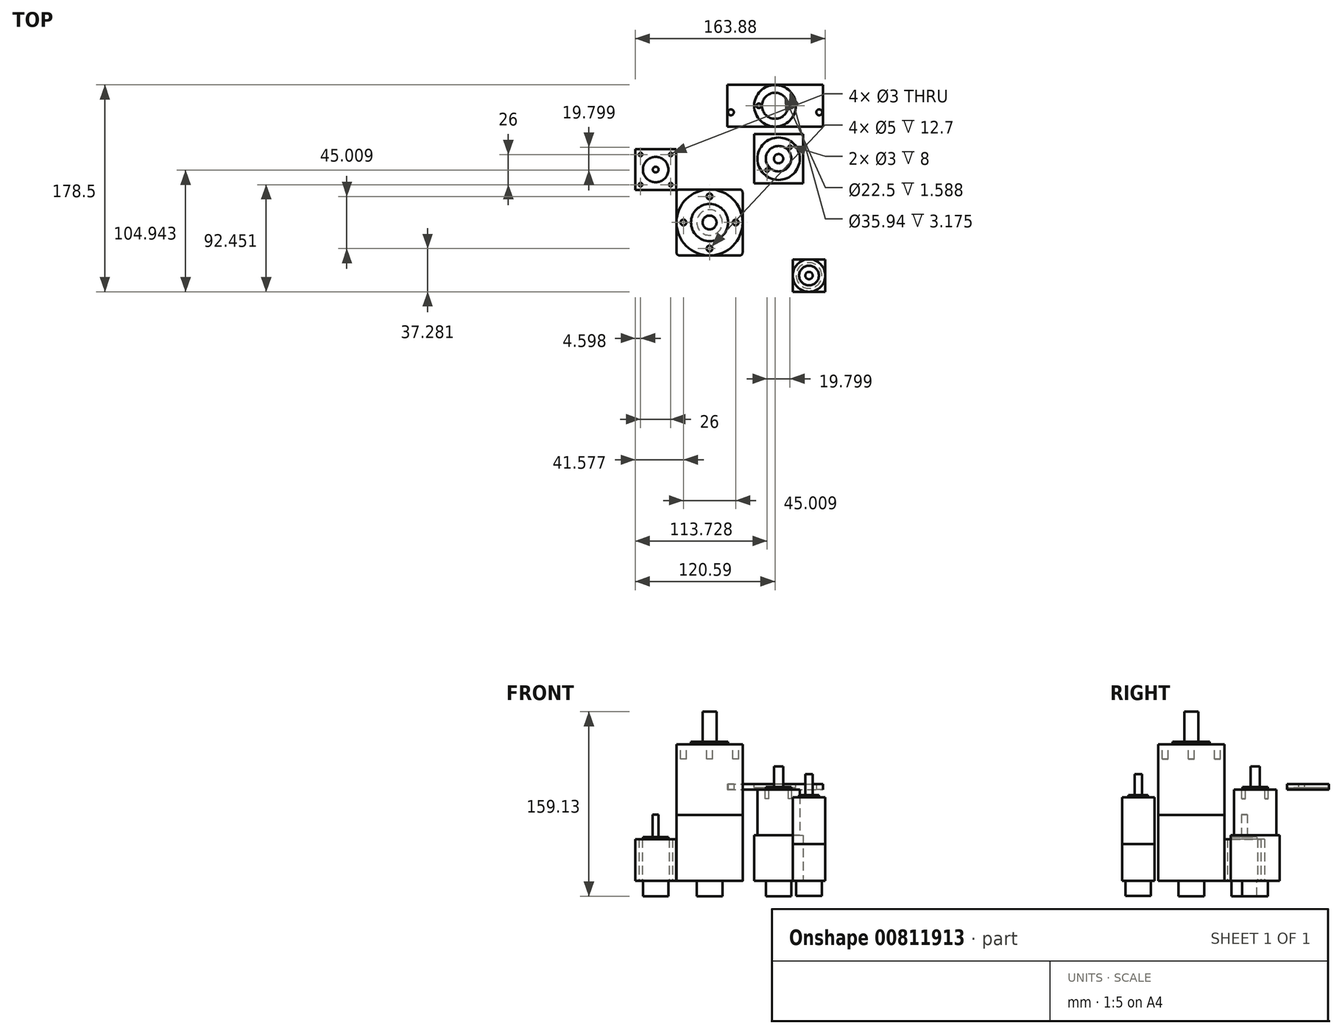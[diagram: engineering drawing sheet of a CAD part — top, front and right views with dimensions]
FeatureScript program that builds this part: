
annotation { "Feature Type Name" : "Feature", "Feature Type Description" : "" }
export const myFeature = defineFeature(function(context is Context, id is Id, definition is map)
    precondition{}
    {
        {
            var Q0;
            Q0=qCreatedBy(makeId("Top.planeOp"),FACE);
            var sketch = newSketch(context, id + "F0", { "sketchPlane" : qUnion([Q0])});
            skLineSegment(sketch, "E0.bottom", {"start": v(-20.35, 13.53) * mm, "end": v(31.57, 13.53) * mm});
            skLineSegment(sketch, "E0.top", {"start": v(-20.35, -43.46) * mm, "end": v(31.57, -43.46) * mm});
            skLineSegment(sketch, "E0.left", {"start": v(-22.89, 11) * mm, "end": v(-22.89, -40.92) * mm});
            skLineSegment(sketch, "E0.right", {"start": v(34.11, 11) * mm, "end": v(34.11, -40.92) * mm});
            skLineSegment(sketch, "E1", {"start": v(-22.89, 13.53) * mm, "end": v(34.11, -43.46) * mm, "construction": true});
            skLineSegment(sketch, "E2", {"start": v(34.11, 13.53) * mm, "end": v(-22.89, -43.46) * mm, "construction": true});
            skCircle(sketch, "E3", {"center": v(5.61, -14.96) * mm, "radius": 28.5 * mm, "construction": true});
            skPoint(sketch, "E4.visualSharp", {"position": v(-22.89, 13.53) * mm});
            skArc(sketch, "E4.filletArc", {"start": v(-20.35, 13.53) * mm, "mid": v(-22.14, 12.8) * mm, "end": v(-22.89, 11) * mm});
            skPoint(sketch, "E5.visualSharp", {"position": v(34.11, 13.53) * mm});
            skArc(sketch, "E5.filletArc", {"start": v(34.11, 11) * mm, "mid": v(33.37, 12.8) * mm, "end": v(31.57, 13.53) * mm});
            skPoint(sketch, "E6.visualSharp", {"position": v(34.11, -43.46) * mm});
            skArc(sketch, "E6.filletArc", {"start": v(31.57, -43.46) * mm, "mid": v(33.37, -42.72) * mm, "end": v(34.11, -40.92) * mm});
            skPoint(sketch, "E7.visualSharp", {"position": v(-22.89, -43.46) * mm});
            skArc(sketch, "E7.filletArc", {"start": v(-22.89, -40.92) * mm, "mid": v(-22.14, -42.72) * mm, "end": v(-20.35, -43.46) * mm});
            skSolve(sketch);
        }
        {
            var Q0;
            Q0=makeQuery(id+"F0.imprint","IMPRINT",FACE,{"disambiguationData":[TD([[makeQuery(id+"F0.imprint","IMPRINT",EDGE,{"derivedFrom":sQuery(id+"F0.wireOp",EDGE,"E0.bottom")}),-1.0]])]});
            extrude(context, id + "F1", {"entities" : qUnion([Q0]), "depth" : 57.02 * mm});
        }
        {
            var Q0;
            Q0=makeQuery(id+"F1.opExtrude","CAP_FACE",FACE,{"disambiguationData":[OSD([sQuery(id+"F0.wireOp",EDGE,"E0.bottom"),sQuery(id+"F0.wireOp",EDGE,"E0.top"),sQuery(id+"F0.wireOp",EDGE,"E0.left"),sQuery(id+"F0.wireOp",EDGE,"E0.right"),sQuery(id+"F0.wireOp",EDGE,"E4.filletArc"),sQuery(id+"F0.wireOp",EDGE,"E5.filletArc"),sQuery(id+"F0.wireOp",EDGE,"E6.filletArc"),sQuery(id+"F0.wireOp",EDGE,"E7.filletArc")])],"isStart":false});
            var sketch = newSketch(context, id + "F2", { "sketchPlane" : qUnion([Q0])});
            skCircle(sketch, "E8", {"center": v(5.61, -14.96) * mm, "radius": 28.5 * mm});
            skSolve(sketch);
        }
        {
            var Q0;
            {var subQ0=sQuery(id+"F2.wireOp",EDGE,"E8");var subQ4=makeQuery(id+"F2.imprint","INTERSECT",VERTEX,{"derivedFrom":[makeQuery(id+"F1.opExtrude","CAP_EDGE",EDGE,{"disambiguationData":[OSD([sQuery(id+"F0.wireOp",EDGE,"E0.bottom")])],"isStart":false}),subQ0]});Q0=makeQuery(id+"F2.imprint","IMPRINT",FACE,{"disambiguationData":[TD([[makeQuery(id+"F2.imprint","IMPRINT",EDGE,{"disambiguationData":[TD([[subQ4,1.0]])],"derivedFrom":subQ0}),1.0]])]});}
            extrude(context, id + "F3", {"entities" : qUnion([Q0]), "operationType" : NewBodyOperationType.ADD, "depth" : 61 * mm});
        }
        {
            var Q0;
            Q0=makeQuery(id+"F3.opExtrude","CAP_FACE",FACE,{"disambiguationData":[OSD([sQuery(id+"F2.wireOp",EDGE,"E8")])],"isStart":false});
            var sketch = newSketch(context, id + "F4", { "sketchPlane" : qUnion([Q0])});
            skCircle(sketch, "E9", {"center": v(5.61, -14.96) * mm, "radius": 16 * mm});
            skSolve(sketch);
        }
        {
            var Q0;
            Q0=makeQuery(id+"F4.imprint","IMPRINT",FACE,{"disambiguationData":[TD([[makeQuery(id+"F4.imprint","IMPRINT",EDGE,{"derivedFrom":sQuery(id+"F4.wireOp",EDGE,"E9")}),1.0]])]});
            extrude(context, id + "F5", {"entities" : qUnion([Q0]), "operationType" : NewBodyOperationType.ADD, "depth" : 2 * mm});
        }
        {
            var Q0;
            Q0=makeQuery(id+"F5.opExtrude","CAP_FACE",FACE,{"disambiguationData":[OSD([sQuery(id+"F4.wireOp",EDGE,"E9")])],"isStart":false});
            var sketch = newSketch(context, id + "F6", { "sketchPlane" : qUnion([Q0])});
            skCircle(sketch, "E10", {"center": v(5.61, -14.96) * mm, "radius": 6 * mm});
            skSolve(sketch);
        }
        {
            var Q0;
            Q0=makeQuery(id+"F6.imprint","IMPRINT",FACE,{"disambiguationData":[TD([[makeQuery(id+"F6.imprint","IMPRINT",EDGE,{"derivedFrom":sQuery(id+"F6.wireOp",EDGE,"E10")}),1.0]])]});
            extrude(context, id + "F7", {"entities" : qUnion([Q0]), "operationType" : NewBodyOperationType.ADD, "depth" : 26 * mm});
        }
        {
            var Q0;
            Q0=makeQuery(id+"F3.opExtrude","CAP_FACE",FACE,{"disambiguationData":[OSD([sQuery(id+"F2.wireOp",EDGE,"E8")])],"isStart":false});
            var sketch = newSketch(context, id + "F8", { "sketchPlane" : qUnion([Q0])});
            skCircle(sketch, "E11", {"center": v(5.61, -14.96) * mm, "radius": 22.5 * mm, "construction": true});
            skCircle(sketch, "E12", {"center": v(5.61, 7.54) * mm, "radius": 2.5 * mm});
            skCircle(sketch, "E13", {"center": v(28.12, -14.96) * mm, "radius": 2.5 * mm});
            skCircle(sketch, "E14", {"center": v(5.61, -37.47) * mm, "radius": 2.5 * mm});
            skCircle(sketch, "E15", {"center": v(-16.9, -14.96) * mm, "radius": 2.5 * mm});
            skSolve(sketch);
        }
        {
            var Q0;
            {Q0=qUnion([makeQuery(id+"F8.imprint","IMPRINT",FACE,{"disambiguationData":[TD([[makeQuery(id+"F8.imprint","IMPRINT",EDGE,{"derivedFrom":sQuery(id+"F8.wireOp",EDGE,"E12")}),1.0]])]}),makeQuery(id+"F8.imprint","IMPRINT",FACE,{"disambiguationData":[TD([[makeQuery(id+"F8.imprint","IMPRINT",EDGE,{"derivedFrom":sQuery(id+"F8.wireOp",EDGE,"E13")}),1.0]])]}),makeQuery(id+"F8.imprint","IMPRINT",FACE,{"disambiguationData":[TD([[makeQuery(id+"F8.imprint","IMPRINT",EDGE,{"derivedFrom":sQuery(id+"F8.wireOp",EDGE,"E14")}),1.0]])]}),makeQuery(id+"F8.imprint","IMPRINT",FACE,{"disambiguationData":[TD([[makeQuery(id+"F8.imprint","IMPRINT",EDGE,{"derivedFrom":sQuery(id+"F8.wireOp",EDGE,"E15")}),1.0]])]})]);}
            extrude(context, id + "F9", {"entities" : qUnion([Q0]), "operationType" : NewBodyOperationType.REMOVE, "oppositeDirection" : true, "depth" : 12.7 * mm});
        }
        {
            var Q0;
            Q0=qCreatedBy(makeId("Top.planeOp"),FACE);
            var sketch = newSketch(context, id + "F10", { "sketchPlane" : qUnion([Q0])});
            skLineSegment(sketch, "E16.bottom", {"start": v(44.01, 61.24) * mm, "end": v(86.3, 61.24) * mm});
            skLineSegment(sketch, "E16.top", {"start": v(44.01, 18.95) * mm, "end": v(86.3, 18.95) * mm});
            skLineSegment(sketch, "E16.left", {"start": v(44.01, 61.24) * mm, "end": v(44.01, 18.95) * mm});
            skLineSegment(sketch, "E16.right", {"start": v(86.3, 61.24) * mm, "end": v(86.3, 18.95) * mm});
            skSolve(sketch);
        }
        {
            var Q0;
            Q0=makeQuery(id+"F10.imprint","IMPRINT",FACE,{"disambiguationData":[TD([[makeQuery(id+"F10.imprint","IMPRINT",EDGE,{"derivedFrom":sQuery(id+"F10.wireOp",EDGE,"E16.bottom")}),-1.0]])]});
            extrude(context, id + "F11", {"entities" : qUnion([Q0]), "depth" : 39.5 * mm});
        }
        {
            var Q0;
            Q0=makeQuery(id+"F11.opExtrude","CAP_FACE",FACE,{"disambiguationData":[OSD([sQuery(id+"F10.wireOp",EDGE,"E16.bottom"),sQuery(id+"F10.wireOp",EDGE,"E16.top"),sQuery(id+"F10.wireOp",EDGE,"E16.left"),sQuery(id+"F10.wireOp",EDGE,"E16.right")])],"isStart":false});
            var sketch = newSketch(context, id + "F12", { "sketchPlane" : qUnion([Q0])});
            skCircle(sketch, "E17", {"center": v(65.16, 40.1) * mm, "radius": 21.15 * mm, "construction": true});
            skCircle(sketch, "E18", {"center": v(65.16, 40.1) * mm, "radius": 18.29 * mm});
            skSolve(sketch);
        }
        {
            var Q0;
            Q0=makeQuery(id+"F12.imprint","IMPRINT",FACE,{"disambiguationData":[TD([[makeQuery(id+"F12.imprint","IMPRINT",EDGE,{"derivedFrom":sQuery(id+"F12.wireOp",EDGE,"E18")}),1.0]])]});
            extrude(context, id + "F13", {"entities" : qUnion([Q0]), "operationType" : NewBodyOperationType.ADD, "depth" : 39.5 * mm});
        }
        {
            var Q0;
            Q0=makeQuery(id+"F13.opExtrude","CAP_FACE",FACE,{"disambiguationData":[OSD([sQuery(id+"F12.wireOp",EDGE,"E18")])],"isStart":false});
            var sketch = newSketch(context, id + "F14", { "sketchPlane" : qUnion([Q0])});
            skCircle(sketch, "E19", {"center": v(65.16, 40.1) * mm, "radius": 11 * mm});
            skSolve(sketch);
        }
        {
            var Q0;
            Q0=makeQuery(id+"F14.imprint","IMPRINT",FACE,{"disambiguationData":[TD([[makeQuery(id+"F14.imprint","IMPRINT",EDGE,{"derivedFrom":sQuery(id+"F14.wireOp",EDGE,"E19")}),1.0]])]});
            extrude(context, id + "F15", {"entities" : qUnion([Q0]), "operationType" : NewBodyOperationType.ADD, "depth" : 1.98 * mm});
        }
        {
            var Q0;
            Q0=makeQuery(id+"F15.opExtrude","CAP_FACE",FACE,{"disambiguationData":[OSD([sQuery(id+"F14.wireOp",EDGE,"E19")])],"isStart":false});
            var sketch = newSketch(context, id + "F16", { "sketchPlane" : qUnion([Q0])});
            skCircle(sketch, "E20", {"center": v(65.16, 40.1) * mm, "radius": 4 * mm});
            skSolve(sketch);
        }
        {
            var Q0;
            Q0=makeQuery(id+"F16.imprint","IMPRINT",FACE,{"disambiguationData":[TD([[makeQuery(id+"F16.imprint","IMPRINT",EDGE,{"derivedFrom":sQuery(id+"F16.wireOp",EDGE,"E20")}),1.0]])]});
            extrude(context, id + "F17", {"entities" : qUnion([Q0]), "operationType" : NewBodyOperationType.ADD, "depth" : 18 * mm});
        }
        {
            var Q0;
            Q0=qCreatedBy(makeId("Top.planeOp"),FACE);
            var sketch = newSketch(context, id + "F18", { "sketchPlane" : qUnion([Q0])});
            skLineSegment(sketch, "E21.bottom", {"start": v(77.42, -46.76) * mm, "end": v(105.4, -46.76) * mm});
            skLineSegment(sketch, "E21.top", {"start": v(77.42, -74.75) * mm, "end": v(105.4, -74.75) * mm});
            skLineSegment(sketch, "E21.left", {"start": v(77.42, -46.76) * mm, "end": v(77.42, -74.75) * mm});
            skLineSegment(sketch, "E21.right", {"start": v(105.4, -46.76) * mm, "end": v(105.4, -74.75) * mm});
            skSolve(sketch);
        }
        {
            var Q0;
            Q0=makeQuery(id+"F18.imprint","IMPRINT",FACE,{"disambiguationData":[TD([[makeQuery(id+"F18.imprint","IMPRINT",EDGE,{"derivedFrom":sQuery(id+"F18.wireOp",EDGE,"E21.bottom")}),-1.0]])]});
            extrude(context, id + "F19", {"entities" : qUnion([Q0]), "depth" : 32 * mm});
        }
        {
            var Q0;
            Q0=makeQuery(id+"F19.opExtrude","CAP_FACE",FACE,{"disambiguationData":[OSD([sQuery(id+"F18.wireOp",EDGE,"E21.bottom"),sQuery(id+"F18.wireOp",EDGE,"E21.top"),sQuery(id+"F18.wireOp",EDGE,"E21.left"),sQuery(id+"F18.wireOp",EDGE,"E21.right")])],"isStart":false});
            var sketch = newSketch(context, id + "F20", { "sketchPlane" : qUnion([Q0])});
            skLineSegment(sketch, "E22.0.0", {"start": v(77.42, -46.76) * mm, "end": v(105.4, -46.76) * mm, "construction": true});
            skLineSegment(sketch, "E22.0.1", {"start": v(77.42, -46.76) * mm, "end": v(77.42, -74.75) * mm, "construction": true});
            skLineSegment(sketch, "E22.0.2", {"start": v(77.42, -74.75) * mm, "end": v(105.4, -74.75) * mm, "construction": true});
            skLineSegment(sketch, "E22.0.3", {"start": v(105.4, -46.76) * mm, "end": v(105.4, -74.75) * mm, "construction": true});
            skLineSegment(sketch, "E23", {"start": v(77.42, -46.76) * mm, "end": v(105.4, -74.75) * mm, "construction": true});
            skCircle(sketch, "E24", {"center": v(91.41, -60.75) * mm, "radius": 14 * mm});
            skSolve(sketch);
        }
        {
            var Q0;
            {var subQ0=sQuery(id+"F20.wireOp",EDGE,"E24");var subQ4=makeQuery(id+"F20.imprint","INTERSECT",VERTEX,{"derivedFrom":[makeQuery(id+"F19.opExtrude","CAP_EDGE",EDGE,{"disambiguationData":[OSD([sQuery(id+"F18.wireOp",EDGE,"E21.bottom")])],"isStart":false}),subQ0]});Q0=makeQuery(id+"F20.imprint","IMPRINT",FACE,{"disambiguationData":[TD([[makeQuery(id+"F20.imprint","IMPRINT",EDGE,{"disambiguationData":[TD([[subQ4,1.0]])],"derivedFrom":subQ0}),1.0]])]});}
            extrude(context, id + "F21", {"entities" : qUnion([Q0]), "operationType" : NewBodyOperationType.ADD, "depth" : 40.1 * mm});
        }
        {
            var Q0;
            Q0=makeQuery(id+"F21.opExtrude","CAP_FACE",FACE,{"disambiguationData":[OSD([sQuery(id+"F20.wireOp",EDGE,"E24")])],"isStart":false});
            var sketch = newSketch(context, id + "F22", { "sketchPlane" : qUnion([Q0])});
            skCircle(sketch, "E25", {"center": v(91.41, -60.75) * mm, "radius": 8.5 * mm});
            skSolve(sketch);
        }
        {
            var Q0;
            Q0=makeQuery(id+"F22.imprint","IMPRINT",FACE,{"disambiguationData":[TD([[makeQuery(id+"F22.imprint","IMPRINT",EDGE,{"derivedFrom":sQuery(id+"F22.wireOp",EDGE,"E25")}),1.0]])]});
            extrude(context, id + "F23", {"entities" : qUnion([Q0]), "operationType" : NewBodyOperationType.ADD, "depth" : 1.98 * mm});
        }
        {
            var Q0;
            Q0=makeQuery(id+"F23.opExtrude","CAP_FACE",FACE,{"disambiguationData":[OSD([sQuery(id+"F22.wireOp",EDGE,"E25")])],"isStart":false});
            var sketch = newSketch(context, id + "F24", { "sketchPlane" : qUnion([Q0])});
            skCircle(sketch, "E26", {"center": v(91.41, -60.75) * mm, "radius": 3.18 * mm});
            skSolve(sketch);
        }
        {
            var Q0;
            Q0=makeQuery(id+"F24.imprint","IMPRINT",FACE,{"disambiguationData":[TD([[makeQuery(id+"F24.imprint","IMPRINT",EDGE,{"derivedFrom":sQuery(id+"F24.wireOp",EDGE,"E26")}),1.0]])]});
            extrude(context, id + "F25", {"entities" : qUnion([Q0]), "operationType" : NewBodyOperationType.ADD, "depth" : 18.03 * mm});
        }
        {
            var Q0;
            Q0=qCreatedBy(makeId("Top.planeOp"),FACE);
            var sketch = newSketch(context, id + "F26", { "sketchPlane" : qUnion([Q0])});
            skLineSegment(sketch, "E27.bottom", {"start": v(-58.47, 48.3) * mm, "end": v(-23.27, 48.3) * mm});
            skLineSegment(sketch, "E27.top", {"start": v(-58.47, 13.1) * mm, "end": v(-23.27, 13.1) * mm});
            skLineSegment(sketch, "E27.left", {"start": v(-58.47, 48.3) * mm, "end": v(-58.47, 13.1) * mm});
            skLineSegment(sketch, "E27.right", {"start": v(-23.27, 48.3) * mm, "end": v(-23.27, 13.1) * mm});
            skLineSegment(sketch, "E28.bottom", {"start": v(-53.87, 43.7) * mm, "end": v(-27.87, 43.7) * mm, "construction": true});
            skLineSegment(sketch, "E28.top", {"start": v(-53.87, 17.7) * mm, "end": v(-27.87, 17.7) * mm, "construction": true});
            skLineSegment(sketch, "E28.left", {"start": v(-53.87, 43.7) * mm, "end": v(-53.87, 17.7) * mm, "construction": true});
            skLineSegment(sketch, "E28.right", {"start": v(-27.87, 43.7) * mm, "end": v(-27.87, 17.7) * mm, "construction": true});
            skLineSegment(sketch, "E29", {"start": v(-40.87, 48.3) * mm, "end": v(-40.87, 13.1) * mm, "construction": true});
            skLineSegment(sketch, "E30", {"start": v(-58.47, 30.7) * mm, "end": v(-23.27, 30.7) * mm, "construction": true});
            skCircle(sketch, "E31", {"center": v(-53.87, 43.7) * mm, "radius": 1.5 * mm});
            skCircle(sketch, "E32", {"center": v(-27.87, 43.7) * mm, "radius": 1.5 * mm});
            skCircle(sketch, "E33", {"center": v(-27.87, 17.7) * mm, "radius": 1.5 * mm});
            skCircle(sketch, "E34", {"center": v(-53.87, 17.7) * mm, "radius": 1.5 * mm});
            skSolve(sketch);
        }
        {
            var Q0;
            Q0=makeQuery(id+"F26.imprint","IMPRINT",FACE,{"disambiguationData":[TD([[makeQuery(id+"F26.imprint","IMPRINT",EDGE,{"derivedFrom":sQuery(id+"F26.wireOp",EDGE,"E27.bottom")}),-1.0]])]});
            extrude(context, id + "F27", {"entities" : qUnion([Q0]), "depth" : 36.07 * mm});
        }
        {
            var Q0;
            Q0=makeQuery(id+"F27.opExtrude","CAP_FACE",FACE,{"disambiguationData":[OSD([sQuery(id+"F26.wireOp",EDGE,"E27.bottom"),sQuery(id+"F26.wireOp",EDGE,"E27.top"),sQuery(id+"F26.wireOp",EDGE,"E27.left"),sQuery(id+"F26.wireOp",EDGE,"E27.right")])],"isStart":false});
            var sketch = newSketch(context, id + "F28", { "sketchPlane" : qUnion([Q0])});
            skCircle(sketch, "E35", {"center": v(-40.87, 30.7) * mm, "radius": 11 * mm});
            skLineSegment(sketch, "E36", {"start": v(-58.47, 13.1) * mm, "end": v(-23.27, 48.3) * mm, "construction": true});
            skSolve(sketch);
        }
        {
            var Q0;
            Q0=makeQuery(id+"F28.imprint","IMPRINT",FACE,{"disambiguationData":[TD([[makeQuery(id+"F28.imprint","IMPRINT",EDGE,{"derivedFrom":sQuery(id+"F28.wireOp",EDGE,"E35")}),1.0]])]});
            extrude(context, id + "F29", {"entities" : qUnion([Q0]), "operationType" : NewBodyOperationType.ADD, "depth" : 1.98 * mm});
        }
        {
            var Q0;
            Q0=makeQuery(id+"F29.opExtrude","CAP_FACE",FACE,{"disambiguationData":[OSD([sQuery(id+"F28.wireOp",EDGE,"E35")])],"isStart":false});
            var sketch = newSketch(context, id + "F30", { "sketchPlane" : qUnion([Q0])});
            skCircle(sketch, "E37", {"center": v(-40.87, 30.7) * mm, "radius": 2.5 * mm});
            skSolve(sketch);
        }
        {
            var Q0;
            Q0=makeQuery(id+"F30.imprint","IMPRINT",FACE,{"disambiguationData":[TD([[makeQuery(id+"F30.imprint","IMPRINT",EDGE,{"derivedFrom":sQuery(id+"F30.wireOp",EDGE,"E37")}),1.0]])]});
            extrude(context, id + "F31", {"entities" : qUnion([Q0]), "operationType" : NewBodyOperationType.ADD, "depth" : 19.3 * mm});
        }
        {
            var Q0;
            Q0=makeQuery(id+"F19.opExtrude","CAP_FACE",FACE,{"disambiguationData":[OSD([sQuery(id+"F18.wireOp",EDGE,"E21.bottom"),sQuery(id+"F18.wireOp",EDGE,"E21.top"),sQuery(id+"F18.wireOp",EDGE,"E21.left"),sQuery(id+"F18.wireOp",EDGE,"E21.right")])],"isStart":true});
            var sketch = newSketch(context, id + "F32", { "sketchPlane" : qUnion([Q0])});
            skCircle(sketch, "E38", {"center": v(91.41, 60.75) * mm, "radius": 11.05 * mm});
            skPoint(sketch, "E38.centerSnap0", {"position": v(105.4, 60.75) * mm});
            skPoint(sketch, "E38.centerSnap1", {"position": v(91.41, 74.75) * mm});
            skSolve(sketch);
        }
        {
            var Q0;
            Q0=qSketchRegion(id+"F32",true);
            extrude(context, id + "F33", {"entities" : qUnion([Q0]), "operationType" : NewBodyOperationType.ADD, "depth" : 13 * mm});
        }
        {
            var Q0;
            Q0=makeQuery(id+"F11.opExtrude","CAP_FACE",FACE,{"disambiguationData":[OSD([sQuery(id+"F10.wireOp",EDGE,"E16.bottom"),sQuery(id+"F10.wireOp",EDGE,"E16.top"),sQuery(id+"F10.wireOp",EDGE,"E16.left"),sQuery(id+"F10.wireOp",EDGE,"E16.right")])],"isStart":true});
            var sketch = newSketch(context, id + "F34", { "sketchPlane" : qUnion([Q0])});
            skCircle(sketch, "E39", {"center": v(65.16, -40.1) * mm, "radius": 11.05 * mm});
            skPoint(sketch, "E39.centerSnap0", {"position": v(86.3, -40.1) * mm});
            skPoint(sketch, "E39.centerSnap1", {"position": v(65.16, -18.95) * mm});
            skSolve(sketch);
        }
        {
            var Q0;
            Q0=qSketchRegion(id+"F34",true);
            extrude(context, id + "F35", {"entities" : qUnion([Q0]), "operationType" : NewBodyOperationType.ADD, "depth" : 13.08 * mm});
        }
        {
            var Q0;
            Q0=makeQuery(id+"F1.opExtrude","CAP_FACE",FACE,{"disambiguationData":[OSD([sQuery(id+"F0.wireOp",EDGE,"E0.bottom"),sQuery(id+"F0.wireOp",EDGE,"E0.top"),sQuery(id+"F0.wireOp",EDGE,"E0.left"),sQuery(id+"F0.wireOp",EDGE,"E0.right"),sQuery(id+"F0.wireOp",EDGE,"E4.filletArc"),sQuery(id+"F0.wireOp",EDGE,"E5.filletArc"),sQuery(id+"F0.wireOp",EDGE,"E6.filletArc"),sQuery(id+"F0.wireOp",EDGE,"E7.filletArc")])],"isStart":true});
            var sketch = newSketch(context, id + "F36", { "sketchPlane" : qUnion([Q0])});
            skCircle(sketch, "E40", {"center": v(5.61, 14.96) * mm, "radius": 11.05 * mm});
            skPoint(sketch, "E40.centerSnap0", {"position": v(34.11, 14.96) * mm});
            skPoint(sketch, "E40.centerSnap1", {"position": v(5.61, 43.46) * mm});
            skSolve(sketch);
        }
        {
            var Q0;
            Q0=qSketchRegion(id+"F36",true);
            extrude(context, id + "F37", {"entities" : qUnion([Q0]), "operationType" : NewBodyOperationType.ADD, "depth" : 13.08 * mm});
        }
        {
            var Q0;
            Q0=makeQuery(id+"F27.opExtrude","CAP_FACE",FACE,{"disambiguationData":[OSD([sQuery(id+"F26.wireOp",EDGE,"E27.bottom"),sQuery(id+"F26.wireOp",EDGE,"E27.top"),sQuery(id+"F26.wireOp",EDGE,"E27.left"),sQuery(id+"F26.wireOp",EDGE,"E27.right"),sQuery(id+"F26.wireOp",EDGE,"E31"),sQuery(id+"F26.wireOp",EDGE,"E32"),sQuery(id+"F26.wireOp",EDGE,"E33"),sQuery(id+"F26.wireOp",EDGE,"E34")])],"isStart":true});
            var sketch = newSketch(context, id + "F38", { "sketchPlane" : qUnion([Q0])});
            skCircle(sketch, "E41", {"center": v(-40.87, -30.7) * mm, "radius": 11.05 * mm});
            skPoint(sketch, "E41.centerSnap0", {"position": v(-23.27, -30.7) * mm});
            skPoint(sketch, "E41.centerSnap1", {"position": v(-40.87, -13.1) * mm});
            skSolve(sketch);
        }
        {
            var Q0;
            Q0=qSketchRegion(id+"F38",true);
            extrude(context, id + "F39", {"entities" : qUnion([Q0]), "operationType" : NewBodyOperationType.ADD, "depth" : 13.08 * mm});
        }
        {
            var Q0;
            Q0=makeQuery(id+"F13.opExtrude","CAP_FACE",FACE,{"disambiguationData":[OSD([sQuery(id+"F12.wireOp",EDGE,"E18")])],"isStart":false});
            var sketch = newSketch(context, id + "F40", { "sketchPlane" : qUnion([Q0])});
            skCircle(sketch, "E42", {"center": v(65.16, 40.1) * mm, "radius": 14 * mm, "construction": true});
            skCircle(sketch, "E43", {"center": v(75.06, 50) * mm, "radius": 1.5 * mm});
            skCircle(sketch, "E44", {"center": v(55.26, 30.2) * mm, "radius": 1.5 * mm});
            skLineSegment(sketch, "E45.0.0", {"start": v(86.3, 61.24) * mm, "end": v(44.01, 61.24) * mm, "construction": true});
            skLineSegment(sketch, "E45.0.1", {"start": v(44.01, 61.24) * mm, "end": v(44.01, 18.95) * mm, "construction": true});
            skLineSegment(sketch, "E45.0.2", {"start": v(44.01, 18.95) * mm, "end": v(86.3, 18.95) * mm, "construction": true});
            skLineSegment(sketch, "E45.0.3", {"start": v(86.3, 18.95) * mm, "end": v(86.3, 61.24) * mm, "construction": true});
            skLineSegment(sketch, "E46", {"start": v(86.3, 61.24) * mm, "end": v(44.01, 18.95) * mm, "construction": true});
            skSolve(sketch);
        }
        {
            var Q0;
            Q0=qSketchRegion(id+"F40",true);
            extrude(context, id + "F41", {"entities" : qUnion([Q0]), "operationType" : NewBodyOperationType.REMOVE, "oppositeDirection" : true, "depth" : 8 * mm});
        }
        {
            var Q0;
            Q0=makeQuery(id+"F13.opExtrude","CAP_FACE",FACE,{"disambiguationData":[OSD([sQuery(id+"F12.wireOp",EDGE,"E18")])],"isStart":false});
            var sketch = newSketch(context, id + "F42", { "sketchPlane" : qUnion([Q0])});
            skLineSegment(sketch, "E47.bottom", {"start": v(20.85, 103.75) * mm, "end": v(103.4, 103.75) * mm});
            skLineSegment(sketch, "E47.top", {"start": v(20.85, 67.75) * mm, "end": v(103.4, 67.75) * mm});
            skLineSegment(sketch, "E47.left", {"start": v(20.85, 103.75) * mm, "end": v(20.85, 67.75) * mm});
            skLineSegment(sketch, "E47.right", {"start": v(103.4, 103.75) * mm, "end": v(103.4, 67.75) * mm});
            skCircle(sketch, "E48", {"center": v(62.12, 85.75) * mm, "radius": 11.25 * mm});
            skLineSegment(sketch, "E49", {"start": v(20.85, 85.75) * mm, "end": v(103.4, 85.75) * mm, "construction": true});
            skLineSegment(sketch, "E50", {"start": v(62.12, 103.75) * mm, "end": v(62.12, 67.75) * mm, "construction": true});
            skCircle(sketch, "E51", {"center": v(62.12, 85.75) * mm, "radius": 14 * mm, "construction": true});
            skCircle(sketch, "E52", {"center": v(48.12, 85.75) * mm, "radius": 2 * mm});
            skCircle(sketch, "E53", {"center": v(76.12, 85.75) * mm, "radius": 2 * mm});
            skCircle(sketch, "E54", {"center": v(100.22, 80.13) * mm, "radius": 2.55 * mm});
            skCircle(sketch, "E55", {"center": v(24.02, 80.13) * mm, "radius": 2.55 * mm});
            skSolve(sketch);
        }
        {
            var Q0;
            Q0=qSketchRegion(id+"F42",true);
            extrude(context, id + "F43", {"entities" : qUnion([Q0]), "depth" : 4.76 * mm});
        }
        {
            var Q0;
            Q0=makeQuery(id+"F43.opExtrude","CAP_FACE",FACE,{"disambiguationData":[OSD([sQuery(id+"F42.wireOp",EDGE,"E47.bottom"),sQuery(id+"F42.wireOp",EDGE,"E47.top"),sQuery(id+"F42.wireOp",EDGE,"E47.left"),sQuery(id+"F42.wireOp",EDGE,"E47.right"),sQuery(id+"F42.wireOp",EDGE,"E48"),sQuery(id+"F42.wireOp",EDGE,"E52"),sQuery(id+"F42.wireOp",EDGE,"E53"),sQuery(id+"F42.wireOp",EDGE,"E54"),sQuery(id+"F42.wireOp",EDGE,"E55")])],"isStart":false});
            var sketch = newSketch(context, id + "F44", { "sketchPlane" : qUnion([Q0])});
            skCircle(sketch, "E56", {"center": v(62.12, 85.75) * mm, "radius": 17.97 * mm});
            skSolve(sketch);
        }
        {
            var Q0;
            Q0=qSketchRegion(id+"F44",true);
            extrude(context, id + "F45", {"entities" : qUnion([Q0]), "operationType" : NewBodyOperationType.REMOVE, "oppositeDirection" : true, "depth" : 3.17 * mm});
        }
    });
